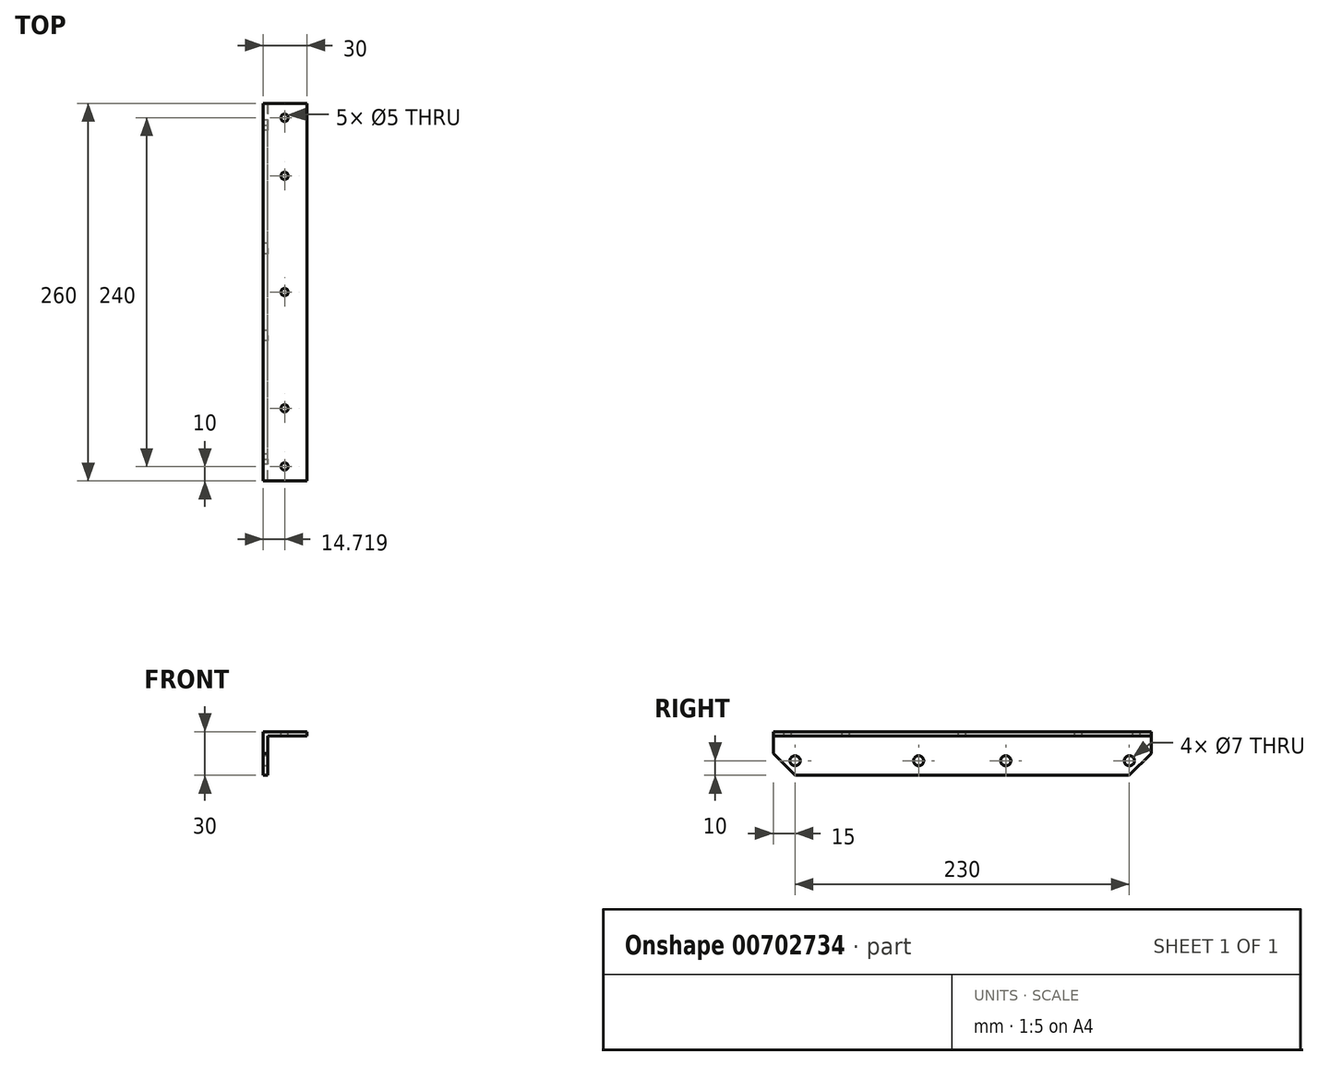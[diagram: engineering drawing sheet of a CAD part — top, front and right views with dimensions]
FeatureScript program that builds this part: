
annotation { "Feature Type Name" : "Feature", "Feature Type Description" : "" }
export const myFeature = defineFeature(function(context is Context, id is Id, definition is map)
    precondition{}
    {
        {
            var Q0;
            Q0=qCreatedBy(makeId("Front.planeOp"),FACE);
            var sketch = newSketch(context, id + "F0", { "sketchPlane" : qUnion([Q0])});
            skLineSegment(sketch, "E0", {"start": v(0, 0) * mm, "end": v(0, 30) * mm});
            skLineSegment(sketch, "E1", {"start": v(0, 30) * mm, "end": v(30, 30) * mm});
            skLineSegment(sketch, "E2", {"start": v(30, 30) * mm, "end": v(30, 27) * mm});
            skLineSegment(sketch, "E3", {"start": v(30, 27) * mm, "end": v(3, 27) * mm});
            skLineSegment(sketch, "E4", {"start": v(3, 27) * mm, "end": v(3, 0) * mm});
            skLineSegment(sketch, "E5", {"start": v(3, 0) * mm, "end": v(0, 0) * mm});
            skSolve(sketch);
        }
        {
            var Q0;
            Q0=makeQuery(id+"F0.imprint","IMPRINT",FACE,{"disambiguationData":[TD([[makeQuery(id+"F0.imprint","IMPRINT",EDGE,{"derivedFrom":sQuery(id+"F0.wireOp",EDGE,"E0")}),-1.0]])]});
            extrude(context, id + "F1", {"entities" : qUnion([Q0]), "endBound" : BoundingType.SYMMETRIC, "depth" : 260 * mm, "offsetDistance" : 25 * mm});
        }
        {
            var Q0;
            Q0=makeQuery(id+"F1.opExtrude","SWEPT_FACE",FACE,{"disambiguationData":[OSD([sQuery(id+"F0.wireOp",EDGE,"E0")])]});
            var sketch = newSketch(context, id + "F2", { "sketchPlane" : qUnion([Q0])});
            skLineSegment(sketch, "E6", {"start": v(0, 30) * mm, "end": v(0, 10) * mm});
            skLineSegment(sketch, "E7", {"start": v(115, 10) * mm, "end": v(130, 10) * mm});
            skLineSegment(sketch, "E8", {"start": v(-115, 10) * mm, "end": v(-130, 10) * mm});
            skLineSegment(sketch, "E9", {"start": v(-115, 10) * mm, "end": v(30, 10) * mm});
            skLineSegment(sketch, "E10", {"start": v(115, 10) * mm, "end": v(-30, 10) * mm});
            skSolve(sketch);
        }
        {
            var Q0;
            Q0=sQuery(id+"F2.wireOp",VERTEX,"h4xNsvRR-XN5t-T3dQ-VFSg-j4WRrjtfRfhr.end");
            var Q1;
            Q1=sQuery(id+"F2.wireOp",VERTEX,"Ygrv8C5C-21mS-Lryx-x8Gy-2dsrVxnptCvR.end");
            var Q2;
            Q2=sQuery(id+"F2.wireOp",VERTEX,"E9.start");
            var Q3;
            Q3=sQuery(id+"F2.wireOp",VERTEX,"E10.end");
            var Q4;
            Q4=sQuery(id+"F2.wireOp",VERTEX,"E9.end");
            var Q5;
            Q5=sQuery(id+"F2.wireOp",VERTEX,"E7.start");
            var Q6;
            Q6=makeQuery(id+"F1.opExtrude","SWEPT_BODY",BODY,{"disambiguationData":[OSD([sQuery(id+"F0.wireOp",EDGE,"E0"),sQuery(id+"F0.wireOp",EDGE,"E1"),sQuery(id+"F0.wireOp",EDGE,"E2"),sQuery(id+"F0.wireOp",EDGE,"E3"),sQuery(id+"F0.wireOp",EDGE,"E4"),sQuery(id+"F0.wireOp",EDGE,"E5")])]});
            hole(context, id + "F3", {"style" : HoleStyle.SIMPLE, "endStyle" : HoleEndStyle.THROUGH, "holeDiameter" : 7 * mm, "majorDiameter" : 5 * mm, "isTappedThrough" : true, "tappedDepth" : 12 * mm, "tapClearance" : 3, "locations" : qUnion([Q0, Q1, Q2, Q3, Q4, Q5]), "scope" : qUnion([Q6])});
        }
        {
            var Q0;
            Q0=makeQuery(id+"F1.opExtrude","SWEPT_FACE",FACE,{"disambiguationData":[OSD([sQuery(id+"F0.wireOp",EDGE,"E1")])]});
            var sketch = newSketch(context, id + "F4", { "sketchPlane" : qUnion([Q0])});
            skLineSegment(sketch, "E11", {"start": v(0, 0) * mm, "end": v(14.72, 0) * mm});
            skLineSegment(sketch, "E12", {"start": v(14.72, 0) * mm, "end": v(14.72, 40) * mm});
            skLineSegment(sketch, "E13", {"start": v(14.72, 0) * mm, "end": v(14.72, -40) * mm});
            skLineSegment(sketch, "E14", {"start": v(14.72, -40) * mm, "end": v(14.72, -80) * mm});
            skLineSegment(sketch, "E15", {"start": v(14.72, -80) * mm, "end": v(14.72, -120) * mm});
            skLineSegment(sketch, "E16", {"start": v(14.72, 40) * mm, "end": v(14.72, 80) * mm});
            skLineSegment(sketch, "E17", {"start": v(14.72, 80) * mm, "end": v(14.72, 120) * mm});
            skSolve(sketch);
        }
        {
            var Q0;
            Q0=sQuery(id+"F4.wireOp",VERTEX,"E15.end");
            var Q1;
            Q1=sQuery(id+"F4.wireOp",VERTEX,"E14.end");
            var Q2;
            Q2=sQuery(id+"F4.wireOp",VERTEX,"E11.end");
            var Q3;
            Q3=sQuery(id+"F4.wireOp",VERTEX,"E16.end");
            var Q4;
            Q4=sQuery(id+"F4.wireOp",VERTEX,"E17.end");
            var Q5;
            Q5=makeQuery(id+"F1.opExtrude","SWEPT_BODY",BODY,{"disambiguationData":[OSD([sQuery(id+"F0.wireOp",EDGE,"E0"),sQuery(id+"F0.wireOp",EDGE,"E1"),sQuery(id+"F0.wireOp",EDGE,"E2"),sQuery(id+"F0.wireOp",EDGE,"E3"),sQuery(id+"F0.wireOp",EDGE,"E4"),sQuery(id+"F0.wireOp",EDGE,"E5")])]});
            hole(context, id + "F5", {"style" : HoleStyle.SIMPLE, "endStyle" : HoleEndStyle.THROUGH, "holeDiameter" : 5 * mm, "majorDiameter" : 5 * mm, "isTappedThrough" : true, "tappedDepth" : 12 * mm, "tapClearance" : 3, "locations" : qUnion([Q0, Q1, Q2, Q3, Q4]), "scope" : qUnion([Q5])});
        }
        {
            var Q0;
            Q0=makeQuery(id+"F1.opExtrude","SWEPT_FACE",FACE,{"disambiguationData":[OSD([sQuery(id+"F0.wireOp",EDGE,"E4")])]});
            var sketch = newSketch(context, id + "F6", { "sketchPlane" : qUnion([Q0])});
            skLineSegment(sketch, "E18", {"start": v(-130, 0) * mm, "end": v(-130, 15) * mm});
            skLineSegment(sketch, "E19", {"start": v(-130, 15) * mm, "end": v(-115, 0) * mm});
            skLineSegment(sketch, "E20", {"start": v(-115, 0) * mm, "end": v(-130, 0) * mm});
            skLineSegment(sketch, "E21", {"start": v(130, 0) * mm, "end": v(130, 15) * mm});
            skLineSegment(sketch, "E22", {"start": v(130, 15) * mm, "end": v(115, 0) * mm});
            skLineSegment(sketch, "E23", {"start": v(115, 0) * mm, "end": v(130, 0) * mm});
            skSolve(sketch);
        }
        {
            var Q0;
            Q0=makeQuery(id+"F6.imprint","IMPRINT",FACE,{"disambiguationData":[TD([[makeQuery(id+"F6.imprint","IMPRINT",EDGE,{"derivedFrom":sQuery(id+"F6.wireOp",EDGE,"E18")}),1.0]])]});
            var Q1;
            Q1=makeQuery(id+"F6.imprint","IMPRINT",FACE,{"disambiguationData":[TD([[makeQuery(id+"F6.imprint","IMPRINT",EDGE,{"derivedFrom":sQuery(id+"F6.wireOp",EDGE,"E21")}),-1.0]])]});
            extrude(context, id + "F7", {"entities" : qUnion([Q0, Q1]), "operationType" : NewBodyOperationType.REMOVE, "oppositeDirection" : true, "depth" : 25 * mm, "offsetDistance" : 25 * mm});
        }
    });
